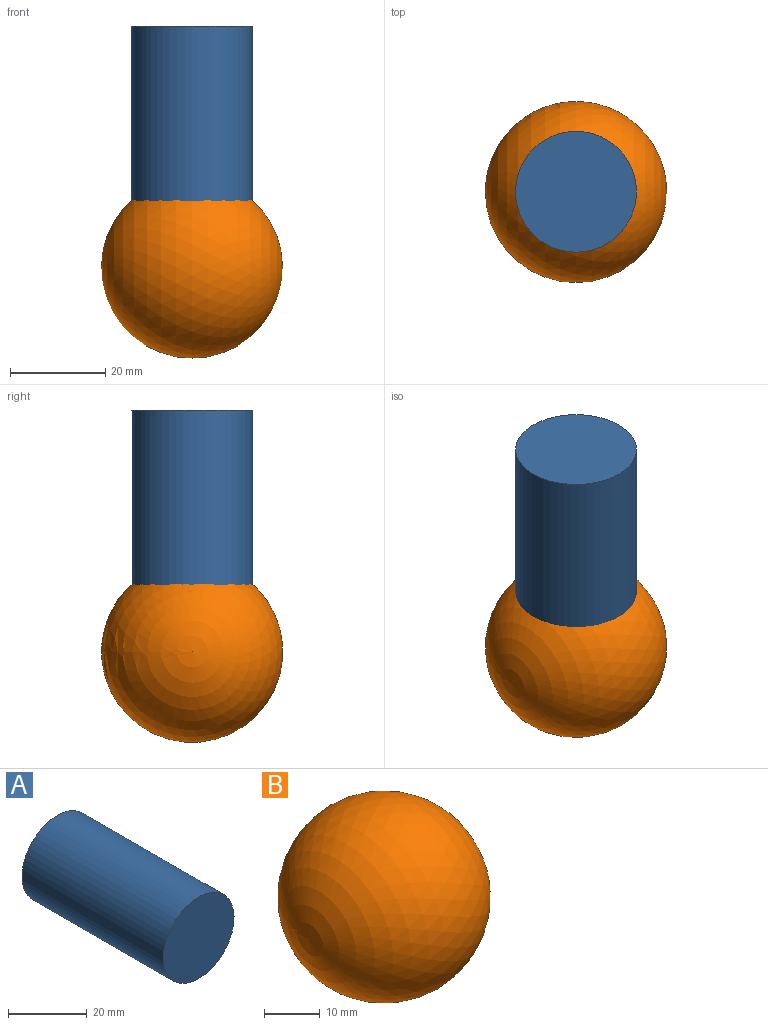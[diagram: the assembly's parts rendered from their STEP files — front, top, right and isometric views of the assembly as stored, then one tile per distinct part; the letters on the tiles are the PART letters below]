
ASSEMBLY  parts=2 mates=1
PART A: 3 faces, bbox 25.4x50.8x25.4 mm
  f0: cylinder r=12.7mm len=50.8mm, axis (0,1,0), area 4053.7mm2, adj f1,f2
  f1: plane 25.4x25.4mm, normal (0,-1,0), area 506.7mm2, adj f0
  f2: plane 25.4x25.4mm, normal (0,1,0), area 506.7mm2, adj f0
PART B: 1 faces, bbox 38.1x38.1x38.1 mm
  f0: sphere r=19.05mm, area 4560.4mm2
PLACE A rot(axis=(-1,0,0),90deg) t=(46.26,-45.84,-8.97)mm
PLACE B t=(34.54,-37.1,-8.97)mm
MATE fastened B.f0 <-> A.f0  axis (0,0,1) through (-5.58,-2.96,-8.97)mm
